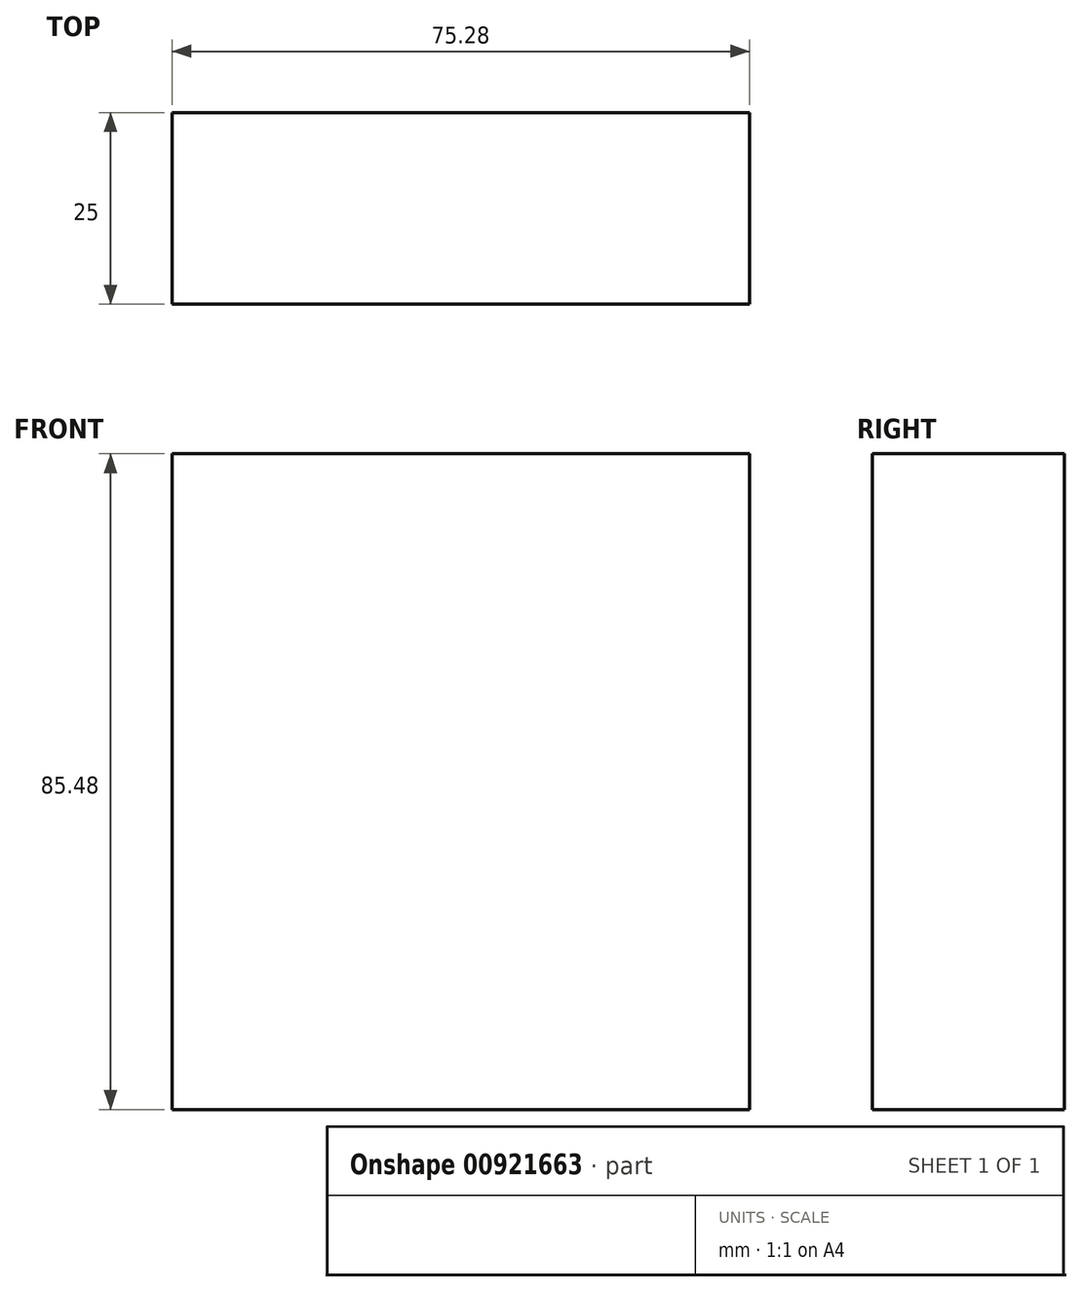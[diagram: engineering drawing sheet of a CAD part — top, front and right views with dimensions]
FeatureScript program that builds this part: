
annotation { "Feature Type Name" : "Feature", "Feature Type Description" : "" }
export const myFeature = defineFeature(function(context is Context, id is Id, definition is map)
    precondition{}
    {
        {
            var Q0;
            Q0=qCreatedBy(makeId("Front.planeOp"),FACE);
            var sketch = newSketch(context, id + "F0", { "sketchPlane" : qUnion([Q0])});
            skLineSegment(sketch, "E0.bottom", {"start": v(-123.04, 45.03) * mm, "end": v(-47.76, 45.03) * mm});
            skLineSegment(sketch, "E0.top", {"start": v(-123.04, -40.45) * mm, "end": v(-47.76, -40.45) * mm});
            skLineSegment(sketch, "E0.left", {"start": v(-123.04, 45.03) * mm, "end": v(-123.04, -40.45) * mm});
            skLineSegment(sketch, "E0.right", {"start": v(-47.76, 45.03) * mm, "end": v(-47.76, -40.45) * mm});
            skSolve(sketch);
        }
        {
            var Q0;
            Q0 = qSketchRegion(id + "F0", true);
            extrude(context, id + "F1", {"entities" : qUnion([Q0]), "depth" : 25 * mm, "offsetDistance" : 25 * mm});
        }
    });
